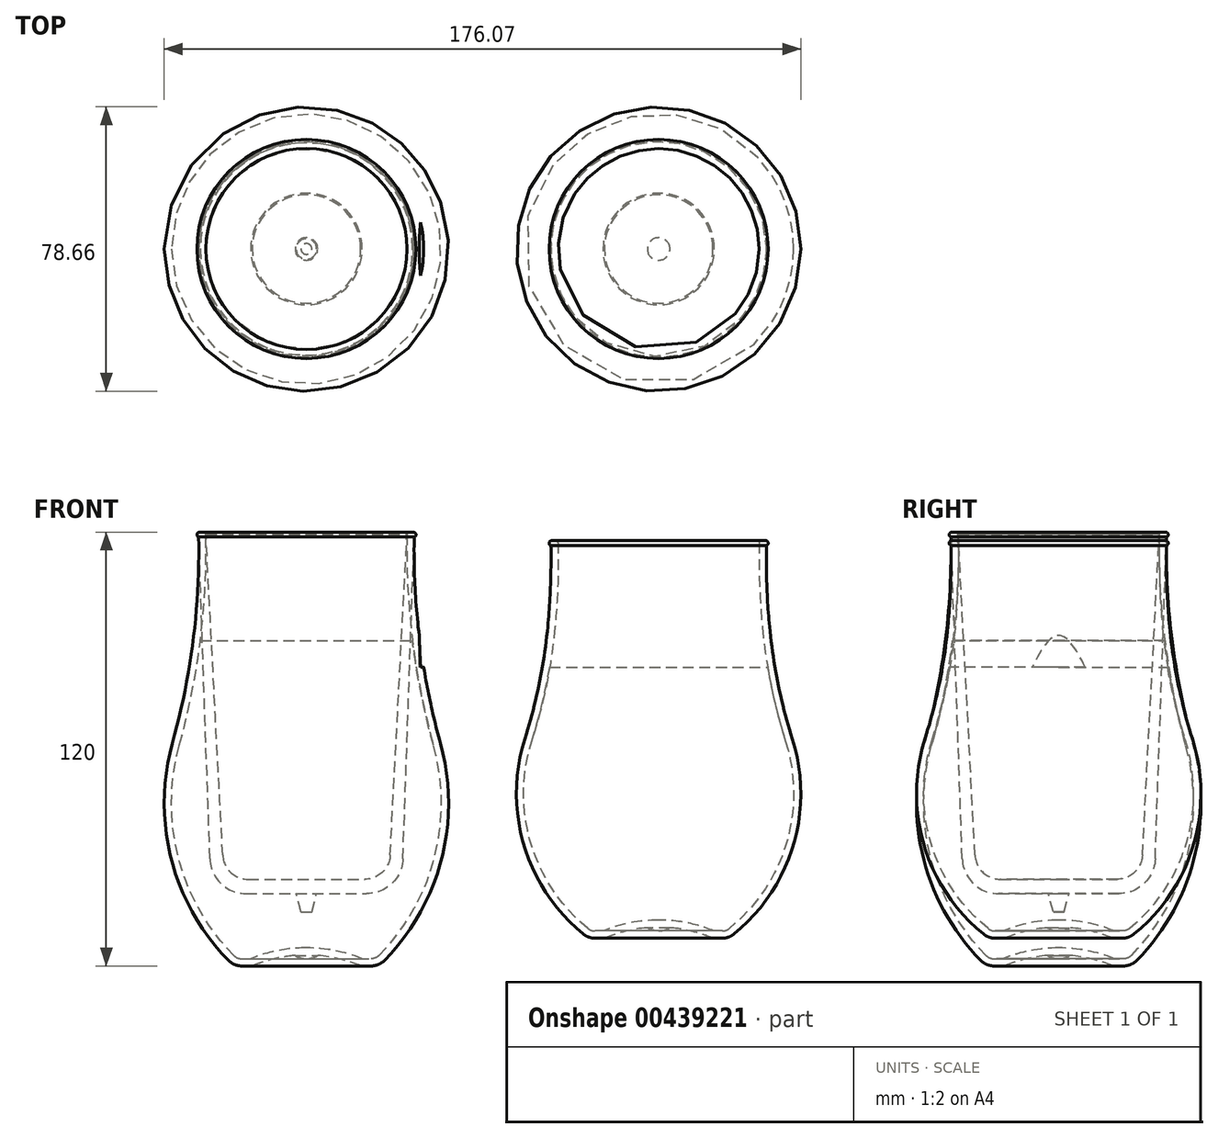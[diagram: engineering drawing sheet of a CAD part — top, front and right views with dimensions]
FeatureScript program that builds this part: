
annotation { "Feature Type Name" : "Feature", "Feature Type Description" : "" }
export const myFeature = defineFeature(function(context is Context, id is Id, definition is map)
    precondition{}
    {
        {
            var Q0;
            Q0=qCreatedBy(makeId("Front.planeOp"),FACE);
            var sketch = newSketch(context, id + "F0", { "sketchPlane" : qUnion([Q0])});
            skLineSegment(sketch, "E0", {"start": v(-17.96, -60) * mm, "end": v(0, -60) * mm});
            skArc(sketch, "E1", {"start": v(-37.07, 1.6) * mm, "mid": v(-37.35, -30.53) * mm, "end": v(-21.52, -58.5) * mm});
            skArc(sketch, "E2", {"start": v(-37.07, 1.6) * mm, "mid": v(-31.37, 29.87) * mm, "end": v(-29.8, 58.66) * mm});
            skArc(sketch, "E3", {"start": v(-21.52, -58.5) * mm, "mid": v(-19.89, -59.61) * mm, "end": v(-17.96, -60) * mm});
            skArc(sketch, "E4", {"start": v(-3.12, -57.12) * mm, "mid": v(-1.62, -57.78) * mm, "end": v(0, -58) * mm});
            skArc(sketch, "E5", {"start": v(-3.12, -57.13) * mm, "mid": v(-9.17, -58.1) * mm, "end": v(-15, -60) * mm});
            skArc(sketch, "E6", {"start": v(-35.14, 1.07) * mm, "mid": v(-29.34, 29.97) * mm, "end": v(-27.81, 59.41) * mm});
            skArc(sketch, "E7", {"start": v(-35.14, 1.07) * mm, "mid": v(-35.42, -30.03) * mm, "end": v(-20.1, -57.1) * mm});
            skArc(sketch, "E8", {"start": v(0, -55) * mm, "mid": v(-7.84, -55.76) * mm, "end": v(-15.4, -58) * mm});
            skLineSegment(sketch, "E9", {"start": v(-17.96, -58) * mm, "end": v(-15.4, -58) * mm});
            skArc(sketch, "E10", {"start": v(-20.1, -57.1) * mm, "mid": v(-19.12, -57.77) * mm, "end": v(-17.96, -58) * mm});
            skArc(sketch, "E11", {"start": v(-30.3, 59.25) * mm, "mid": v(-30.16, 58.86) * mm, "end": v(-29.8, 58.66) * mm});
            skArc(sketch, "E12", {"start": v(-29.55, 60) * mm, "mid": v(-30.08, 59.78) * mm, "end": v(-30.3, 59.25) * mm});
            skArc(sketch, "E13", {"start": v(-27.81, 59.41) * mm, "mid": v(-28, 59.83) * mm, "end": v(-28.41, 60) * mm});
            skLineSegment(sketch, "E14", {"start": v(-29.55, 60) * mm, "end": v(-28.41, 60) * mm});
            skLineSegment(sketch, "E15", {"start": v(-28.41, 60) * mm, "end": v(0, 60) * mm});
            skLineSegment(sketch, "E16", {"start": v(17.96, -60) * mm, "end": v(0, -60) * mm});
            skArc(sketch, "E17", {"start": v(21.52, -58.5) * mm, "mid": v(37.35, -30.53) * mm, "end": v(37.07, 1.6) * mm});
            skArc(sketch, "E18", {"start": v(17.96, -60) * mm, "mid": v(19.89, -59.61) * mm, "end": v(21.52, -58.5) * mm});
            skArc(sketch, "E19", {"start": v(0, -58) * mm, "mid": v(1.62, -57.78) * mm, "end": v(3.12, -57.12) * mm});
            skArc(sketch, "E20", {"start": v(15, -60) * mm, "mid": v(9.17, -58.1) * mm, "end": v(3.12, -57.13) * mm});
            skArc(sketch, "E21", {"start": v(27.81, 59.41) * mm, "mid": v(29.34, 29.97) * mm, "end": v(35.14, 1.07) * mm});
            skArc(sketch, "E22", {"start": v(20.1, -57.1) * mm, "mid": v(35.42, -30.03) * mm, "end": v(35.14, 1.07) * mm});
            skArc(sketch, "E23", {"start": v(15.4, -58) * mm, "mid": v(7.84, -55.76) * mm, "end": v(0, -55) * mm});
            skLineSegment(sketch, "E24", {"start": v(17.96, -58) * mm, "end": v(15.4, -58) * mm});
            skArc(sketch, "E25", {"start": v(17.96, -58) * mm, "mid": v(19.12, -57.77) * mm, "end": v(20.1, -57.1) * mm});
            skArc(sketch, "E26", {"start": v(29.8, 58.66) * mm, "mid": v(30.16, 58.86) * mm, "end": v(30.3, 59.25) * mm});
            skArc(sketch, "E27", {"start": v(30.3, 59.25) * mm, "mid": v(30.08, 59.78) * mm, "end": v(29.55, 60) * mm});
            skArc(sketch, "E28", {"start": v(28.41, 60) * mm, "mid": v(28, 59.83) * mm, "end": v(27.81, 59.41) * mm});
            skLineSegment(sketch, "E29", {"start": v(29.55, 60) * mm, "end": v(28.41, 60) * mm});
            skArc(sketch, "E30", {"start": v(29.8, 58.66) * mm, "mid": v(31.37, 29.87) * mm, "end": v(37.07, 1.6) * mm});
            skLineSegment(sketch, "E31", {"start": v(28.41, 60) * mm, "end": v(0, 60) * mm});
            skSolve(sketch);
        }
        {
            var Q0;
            Q0=qCreatedBy(makeId("Front.planeOp"),FACE);
            var sketch = newSketch(context, id + "F1", { "sketchPlane" : qUnion([Q0])});
            skArc(sketch, "E32.0", {"start": v(-35.14, 1.07) * mm, "mid": v(-29.34, 29.97) * mm, "end": v(-27.81, 59.41) * mm});
            skArc(sketch, "E33.0", {"start": v(-27.81, 59.41) * mm, "mid": v(-28, 59.83) * mm, "end": v(-28.41, 60) * mm});
            skLineSegment(sketch, "E34.0", {"start": v(-28.41, 60) * mm, "end": v(0, 60) * mm});
            skArc(sketch, "E35.0", {"start": v(-35.14, 1.07) * mm, "mid": v(-35.42, -30.03) * mm, "end": v(-20.1, -57.1) * mm});
            skArc(sketch, "E36.0", {"start": v(-20.1, -57.1) * mm, "mid": v(-19.12, -57.77) * mm, "end": v(-17.96, -58) * mm});
            skLineSegment(sketch, "E37.0", {"start": v(-17.96, -58) * mm, "end": v(-15.4, -58) * mm});
            skArc(sketch, "E38.0", {"start": v(0, -55) * mm, "mid": v(-7.84, -55.76) * mm, "end": v(-15.4, -58) * mm});
            skLineSegment(sketch, "E39", {"start": v(0, -55) * mm, "end": v(0, 60) * mm});
            skSolve(sketch);
        }
        {
            var Q0;
            Q0 = qSketchRegion(id + "F1", true);
            var Q1;
            Q1=sQuery(id+"F1.wireOp",EDGE,"E39");
            revolve(context, id + "F2", {"entities" : qUnion([Q0]), "axis" : qUnion([Q1]), "revolveType" : RevolveType.FULL});
        }
        {
            var Q0;
            Q0=makeQuery(id+"F2.opRevolve","SWEPT_FACE",FACE,{"disambiguationData":[OSD([sQuery(id+"F1.wireOp",EDGE,"E34.0")])]});
            var sketch = newSketch(context, id + "F3", { "sketchPlane" : qUnion([Q0])});
            skCircle(sketch, "E40", {"center": v(0, 0) * mm, "radius": 125.99 * mm});
            skSolve(sketch);
        }
        {
            var Q0;
            Q0 = qSketchRegion(id + "F3", true);
            extrude(context, id + "F4", {"entities" : qUnion([Q0]), "operationType" : NewBodyOperationType.REMOVE, "oppositeDirection" : true, "depth" : 30 * mm});
        }
        {
            var Q0;
            Q0=qCreatedBy(makeId("Front.planeOp"),FACE);
            var sketch = newSketch(context, id + "F5", { "sketchPlane" : qUnion([Q0])});
            skArc(sketch, "E41.0", {"start": v(-27.81, 59.41) * mm, "mid": v(-28, 59.83) * mm, "end": v(-28.41, 60) * mm});
            skLineSegment(sketch, "E42.0", {"start": v(-29.55, 60) * mm, "end": v(-28.41, 60) * mm});
            skArc(sketch, "E43.0", {"start": v(-29.55, 60) * mm, "mid": v(-30.08, 59.78) * mm, "end": v(-30.3, 59.25) * mm});
            skArc(sketch, "E44.0", {"start": v(-30.3, 59.25) * mm, "mid": v(-30.16, 58.86) * mm, "end": v(-29.8, 58.66) * mm});
            skArc(sketch, "E45.0", {"start": v(-37.07, 1.6) * mm, "mid": v(-31.37, 29.87) * mm, "end": v(-29.8, 58.66) * mm});
            skArc(sketch, "E46.0", {"start": v(-35.14, 1.07) * mm, "mid": v(-29.34, 29.97) * mm, "end": v(-27.81, 59.41) * mm});
            skArc(sketch, "E47.0", {"start": v(-35.14, 1.07) * mm, "mid": v(-35.42, -30.03) * mm, "end": v(-20.1, -57.1) * mm});
            skArc(sketch, "E48.0", {"start": v(-37.07, 1.6) * mm, "mid": v(-37.35, -30.53) * mm, "end": v(-21.52, -58.5) * mm});
            skArc(sketch, "E49.0", {"start": v(-20.1, -57.1) * mm, "mid": v(-19.12, -57.77) * mm, "end": v(-17.96, -58) * mm});
            skArc(sketch, "E50.0", {"start": v(-21.52, -58.5) * mm, "mid": v(-19.89, -59.61) * mm, "end": v(-17.96, -60) * mm});
            skLineSegment(sketch, "E51.0", {"start": v(-17.96, -58) * mm, "end": v(-15.4, -58) * mm});
            skArc(sketch, "E52.0", {"start": v(0, -55) * mm, "mid": v(-7.84, -55.76) * mm, "end": v(-15.4, -58) * mm});
            skArc(sketch, "E53.0", {"start": v(-3.12, -57.13) * mm, "mid": v(-9.17, -58.1) * mm, "end": v(-15, -60) * mm});
            skArc(sketch, "E54.0", {"start": v(-3.12, -57.12) * mm, "mid": v(-1.62, -57.78) * mm, "end": v(0, -58) * mm});
            skLineSegment(sketch, "E55", {"start": v(-17.96, -60) * mm, "end": v(-15, -60) * mm});
            skLineSegment(sketch, "E56", {"start": v(0, -58) * mm, "end": v(0, -55) * mm});
            skSolve(sketch);
        }
        {
            var Q0;
            Q0 = qSketchRegion(id + "F5", true);
            var Q1;
            Q1=sQuery(id+"F5.wireOp",EDGE,"E56");
            revolve(context, id + "F6", {"entities" : qUnion([Q0]), "axis" : qUnion([Q1]), "revolveType" : RevolveType.FULL});
        }
        {
            var Q0;
            Q0=qCreatedBy(makeId("Front.planeOp"),FACE);
            var sketch = newSketch(context, id + "F7", { "sketchPlane" : qUnion([Q0])});
            skArc(sketch, "E57.0", {"start": v(-27.81, 59.41) * mm, "mid": v(-28, 59.83) * mm, "end": v(-28.41, 60) * mm});
            skLineSegment(sketch, "E58.0", {"start": v(-29.55, 60) * mm, "end": v(-28.41, 60) * mm});
            skArc(sketch, "E59.0", {"start": v(-29.55, 60) * mm, "mid": v(-30.08, 59.78) * mm, "end": v(-30.3, 59.25) * mm});
            skArc(sketch, "E60.0", {"start": v(-30.3, 59.25) * mm, "mid": v(-30.16, 58.86) * mm, "end": v(-29.8, 58.66) * mm});
            skLineSegment(sketch, "E61", {"start": v(-29.8, 58.66) * mm, "end": v(-26.7, -30.35) * mm});
            skLineSegment(sketch, "E62", {"start": v(-16.7, -40) * mm, "end": v(-2.84, -40) * mm});
            skLineSegment(sketch, "E63", {"start": v(0, -40) * mm, "end": v(0, -36) * mm});
            skLineSegment(sketch, "E64", {"start": v(0, -36) * mm, "end": v(-16.17, -36) * mm});
            skLineSegment(sketch, "E65", {"start": v(-23.16, -29.37) * mm, "end": v(-27.81, 59.41) * mm});
            skLineSegment(sketch, "E66", {"start": v(0, -40) * mm, "end": v(0, -45) * mm});
            skLineSegment(sketch, "E67", {"start": v(0, -45) * mm, "end": v(-1.5, -45) * mm});
            skLineSegment(sketch, "E68", {"start": v(-1.5, -45) * mm, "end": v(-2.84, -40) * mm});
            skPoint(sketch, "E69.visualSharp", {"position": v(-22.81, -36) * mm});
            skArc(sketch, "E69.filletArc", {"start": v(-23.16, -29.37) * mm, "mid": v(-21, -34.08) * mm, "end": v(-16.17, -36) * mm});
            skPoint(sketch, "E70.visualSharp", {"position": v(-26.36, -40) * mm});
            skArc(sketch, "E70.filletArc", {"start": v(-26.7, -30.35) * mm, "mid": v(-23.65, -37.2) * mm, "end": v(-16.7, -40) * mm});
            skSolve(sketch);
        }
        {
            var Q0;
            Q0 = qSketchRegion(id + "F7", true);
            var Q1;
            Q1=sQuery(id+"F7.wireOp",EDGE,"E63");
            revolve(context, id + "F8", {"entities" : qUnion([Q0]), "axis" : qUnion([Q1]), "revolveType" : RevolveType.FULL});
        }
        {
            var Q0;
            Q0=qCreatedBy(makeId("Front.planeOp"),FACE);
            var sketch = newSketch(context, id + "F9", { "sketchPlane" : qUnion([Q0])});
            skLineSegment(sketch, "E71", {"start": v(-115.37, -60) * mm, "end": v(-97.41, -60) * mm});
            skArc(sketch, "E72", {"start": v(-134.48, 1.6) * mm, "mid": v(-134.77, -30.53) * mm, "end": v(-118.94, -58.5) * mm});
            skArc(sketch, "E73", {"start": v(-134.48, 1.6) * mm, "mid": v(-128.79, 29.87) * mm, "end": v(-127.22, 58.66) * mm});
            skArc(sketch, "E74", {"start": v(-118.94, -58.5) * mm, "mid": v(-117.3, -59.61) * mm, "end": v(-115.37, -60) * mm});
            skArc(sketch, "E75", {"start": v(-100.53, -57.12) * mm, "mid": v(-99.03, -57.78) * mm, "end": v(-97.41, -58) * mm});
            skArc(sketch, "E76", {"start": v(-100.53, -57.13) * mm, "mid": v(-106.59, -58.1) * mm, "end": v(-112.41, -60) * mm});
            skArc(sketch, "E77", {"start": v(-132.55, 1.07) * mm, "mid": v(-126.76, 29.97) * mm, "end": v(-125.23, 59.41) * mm});
            skArc(sketch, "E78", {"start": v(-132.55, 1.07) * mm, "mid": v(-132.83, -30.03) * mm, "end": v(-117.5, -57.1) * mm});
            skArc(sketch, "E79", {"start": v(-97.41, -55) * mm, "mid": v(-105.26, -55.76) * mm, "end": v(-112.8, -58) * mm});
            skLineSegment(sketch, "E80", {"start": v(-115.37, -58) * mm, "end": v(-112.8, -58) * mm});
            skArc(sketch, "E81", {"start": v(-117.5, -57.1) * mm, "mid": v(-116.53, -57.77) * mm, "end": v(-115.37, -58) * mm});
            skArc(sketch, "E82", {"start": v(-127.71, 59.25) * mm, "mid": v(-127.57, 58.86) * mm, "end": v(-127.22, 58.66) * mm});
            skArc(sketch, "E83", {"start": v(-126.96, 60) * mm, "mid": v(-127.5, 59.78) * mm, "end": v(-127.71, 59.25) * mm});
            skArc(sketch, "E84", {"start": v(-125.23, 59.41) * mm, "mid": v(-125.4, 59.83) * mm, "end": v(-125.83, 60) * mm});
            skLineSegment(sketch, "E85", {"start": v(-126.96, 60) * mm, "end": v(-125.83, 60) * mm});
            skLineSegment(sketch, "E86", {"start": v(-125.83, 60) * mm, "end": v(-97.41, 60) * mm});
            skLineSegment(sketch, "E87", {"start": v(-79.46, -60) * mm, "end": v(-97.41, -60) * mm});
            skArc(sketch, "E88", {"start": v(-75.9, -58.5) * mm, "mid": v(-60.06, -30.53) * mm, "end": v(-60.35, 1.6) * mm});
            skArc(sketch, "E89", {"start": v(-79.46, -60) * mm, "mid": v(-77.53, -59.61) * mm, "end": v(-75.9, -58.5) * mm});
            skArc(sketch, "E90", {"start": v(-97.41, -58) * mm, "mid": v(-95.8, -57.78) * mm, "end": v(-94.3, -57.12) * mm});
            skArc(sketch, "E91", {"start": v(-82.41, -60) * mm, "mid": v(-88.24, -58.1) * mm, "end": v(-94.3, -57.13) * mm});
            skArc(sketch, "E92", {"start": v(-69.6, 59.41) * mm, "mid": v(-68.07, 29.97) * mm, "end": v(-62.27, 1.07) * mm});
            skArc(sketch, "E93", {"start": v(-77.32, -57.1) * mm, "mid": v(-62, -30.03) * mm, "end": v(-62.27, 1.07) * mm});
            skArc(sketch, "E94", {"start": v(-82.02, -58) * mm, "mid": v(-89.57, -55.76) * mm, "end": v(-97.41, -55) * mm});
            skLineSegment(sketch, "E95", {"start": v(-79.46, -58) * mm, "end": v(-82.02, -58) * mm});
            skArc(sketch, "E96", {"start": v(-79.46, -58) * mm, "mid": v(-78.3, -57.77) * mm, "end": v(-77.32, -57.1) * mm});
            skArc(sketch, "E97", {"start": v(-67.61, 58.66) * mm, "mid": v(-67.26, 58.86) * mm, "end": v(-67.12, 59.25) * mm});
            skArc(sketch, "E98", {"start": v(-67.12, 59.25) * mm, "mid": v(-67.34, 59.78) * mm, "end": v(-67.87, 60) * mm});
            skArc(sketch, "E99", {"start": v(-69, 60) * mm, "mid": v(-69.42, 59.83) * mm, "end": v(-69.6, 59.41) * mm});
            skLineSegment(sketch, "E100", {"start": v(-67.87, 60) * mm, "end": v(-69, 60) * mm});
            skArc(sketch, "E101", {"start": v(-67.61, 58.66) * mm, "mid": v(-66.04, 29.87) * mm, "end": v(-60.35, 1.6) * mm});
            skLineSegment(sketch, "E102", {"start": v(-69, 60) * mm, "end": v(-97.41, 60) * mm});
            skLineSegment(sketch, "E103", {"start": v(-68.07, 30) * mm, "end": v(-126.75, 30) * mm});
            skLineSegment(sketch, "E104", {"start": v(-123.76, -40.35) * mm, "end": v(-127.22, 58.66) * mm});
            skLineSegment(sketch, "E105", {"start": v(-113.76, -50) * mm, "end": v(-100.25, -50) * mm});
            skArc(sketch, "E106", {"start": v(-123.76, -40.35) * mm, "mid": v(-120.71, -47.2) * mm, "end": v(-113.76, -50) * mm});
            skLineSegment(sketch, "E107", {"start": v(-113.5, -46) * mm, "end": v(-97.41, -46) * mm});
            skLineSegment(sketch, "E108", {"start": v(-100.25, -50) * mm, "end": v(-98.91, -55) * mm});
            skLineSegment(sketch, "E109", {"start": v(-98.91, -55) * mm, "end": v(-97.41, -55) * mm});
            skLineSegment(sketch, "E110", {"start": v(-120.49, -39.34) * mm, "end": v(-125.23, 59.45) * mm});
            skArc(sketch, "E111", {"start": v(-120.49, -39.34) * mm, "mid": v(-118.32, -44.07) * mm, "end": v(-113.5, -46) * mm});
            skArc(sketch, "E112", {"start": v(94.3, -49.45) * mm, "mid": v(95.8, -50.1) * mm, "end": v(97.41, -50.32) * mm});
            skArc(sketch, "E113", {"start": v(94.3, -49.45) * mm, "mid": v(88.24, -50.42) * mm, "end": v(82.41, -52.32) * mm});
            skArc(sketch, "E114", {"start": v(97.41, -47.32) * mm, "mid": v(89.57, -48.08) * mm, "end": v(82.02, -50.32) * mm});
            skLineSegment(sketch, "E115", {"start": v(79.77, -50.32) * mm, "end": v(82.02, -50.32) * mm});
            skArc(sketch, "E116", {"start": v(67.12, 56.93) * mm, "mid": v(67.26, 56.54) * mm, "end": v(67.61, 56.33) * mm});
            skArc(sketch, "E117", {"start": v(67.87, 57.68) * mm, "mid": v(67.34, 57.46) * mm, "end": v(67.12, 56.93) * mm});
            skArc(sketch, "E118", {"start": v(66.74, 33.85) * mm, "mid": v(67.5, 45.08) * mm, "end": v(67.61, 56.33) * mm});
            skLineSegment(sketch, "E119", {"start": v(79.77, -52.32) * mm, "end": v(82.41, -52.32) * mm});
            skArc(sketch, "E120", {"start": v(60.42, 2.78) * mm, "mid": v(60.2, -26.71) * mm, "end": v(76.63, -51.2) * mm});
            skArc(sketch, "E121", {"start": v(76.63, -51.2) * mm, "mid": v(78.1, -52.04) * mm, "end": v(79.77, -52.32) * mm});
            skArc(sketch, "E122", {"start": v(60.42, 2.78) * mm, "mid": v(64.4, 18.15) * mm, "end": v(66.74, 33.85) * mm});
            skArc(sketch, "E123", {"start": v(68.74, 33.66) * mm, "mid": v(69.5, 45.36) * mm, "end": v(69.6, 57.09) * mm});
            skArc(sketch, "E124", {"start": v(62.33, 2.18) * mm, "mid": v(66.37, 17.75) * mm, "end": v(68.74, 33.66) * mm});
            skArc(sketch, "E125", {"start": v(62.33, 2.18) * mm, "mid": v(62.11, -26.14) * mm, "end": v(77.89, -49.66) * mm});
            skArc(sketch, "E126", {"start": v(77.89, -49.66) * mm, "mid": v(78.77, -50.15) * mm, "end": v(79.77, -50.32) * mm});
            skArc(sketch, "E127", {"start": v(69.6, 57.09) * mm, "mid": v(69.42, 57.5) * mm, "end": v(69, 57.68) * mm});
            skLineSegment(sketch, "E128", {"start": v(67.87, 57.68) * mm, "end": v(69, 57.68) * mm});
            skLineSegment(sketch, "E129", {"start": v(69, 57.68) * mm, "end": v(97.41, 57.68) * mm});
            skArc(sketch, "E130", {"start": v(127.22, 56.33) * mm, "mid": v(127.57, 56.54) * mm, "end": v(127.71, 56.93) * mm});
            skArc(sketch, "E131", {"start": v(127.71, 56.93) * mm, "mid": v(127.5, 57.46) * mm, "end": v(126.96, 57.68) * mm});
            skArc(sketch, "E132", {"start": v(127.22, 56.33) * mm, "mid": v(127.33, 45.08) * mm, "end": v(128.08, 33.85) * mm});
            skArc(sketch, "E133", {"start": v(125.23, 57.09) * mm, "mid": v(125.32, 45.36) * mm, "end": v(126.1, 33.66) * mm});
            skArc(sketch, "E134", {"start": v(125.83, 57.68) * mm, "mid": v(125.4, 57.5) * mm, "end": v(125.23, 57.09) * mm});
            skLineSegment(sketch, "E135", {"start": v(126.96, 57.68) * mm, "end": v(125.83, 57.68) * mm});
            skLineSegment(sketch, "E136", {"start": v(125.83, 57.68) * mm, "end": v(97.41, 57.68) * mm});
            skArc(sketch, "E137", {"start": v(118.2, -51.2) * mm, "mid": v(134.63, -26.71) * mm, "end": v(134.4, 2.78) * mm});
            skArc(sketch, "E138", {"start": v(128.08, 33.85) * mm, "mid": v(130.42, 18.15) * mm, "end": v(134.4, 2.78) * mm});
            skArc(sketch, "E139", {"start": v(126.1, 33.66) * mm, "mid": v(128.46, 17.75) * mm, "end": v(132.5, 2.18) * mm});
            skArc(sketch, "E140", {"start": v(116.94, -49.66) * mm, "mid": v(132.72, -26.14) * mm, "end": v(132.5, 2.18) * mm});
            skArc(sketch, "E141", {"start": v(97.41, -50.32) * mm, "mid": v(99.03, -50.1) * mm, "end": v(100.53, -49.45) * mm});
            skArc(sketch, "E142", {"start": v(112.41, -52.32) * mm, "mid": v(106.59, -50.42) * mm, "end": v(100.53, -49.45) * mm});
            skArc(sketch, "E143", {"start": v(112.8, -50.32) * mm, "mid": v(105.26, -48.08) * mm, "end": v(97.41, -47.32) * mm});
            skLineSegment(sketch, "E144", {"start": v(115.06, -52.32) * mm, "end": v(112.41, -52.32) * mm});
            skArc(sketch, "E145", {"start": v(115.06, -52.32) * mm, "mid": v(116.72, -52.04) * mm, "end": v(118.2, -51.2) * mm});
            skArc(sketch, "E146", {"start": v(115.06, -50.32) * mm, "mid": v(116.06, -50.15) * mm, "end": v(116.94, -49.66) * mm});
            skLineSegment(sketch, "E147", {"start": v(115.06, -50.32) * mm, "end": v(112.8, -50.32) * mm});
            skLineSegment(sketch, "E148", {"start": v(82.41, -52.32) * mm, "end": v(112.41, -52.32) * mm});
            skSolve(sketch);
        }
        {
            var Q0;
            Q0=qCreatedBy(makeId("Front.planeOp"),FACE);
            var sketch = newSketch(context, id + "F10", { "sketchPlane" : qUnion([Q0])});
            skArc(sketch, "E149.0", {"start": v(69.6, 57.09) * mm, "mid": v(69.42, 57.5) * mm, "end": v(69, 57.68) * mm});
            skArc(sketch, "E150.0", {"start": v(68.74, 33.66) * mm, "mid": v(69.5, 45.36) * mm, "end": v(69.6, 57.09) * mm});
            skArc(sketch, "E151.0", {"start": v(62.33, 2.18) * mm, "mid": v(66.37, 17.75) * mm, "end": v(68.74, 33.66) * mm});
            skArc(sketch, "E152.0", {"start": v(62.33, 2.18) * mm, "mid": v(62.11, -26.14) * mm, "end": v(77.89, -49.66) * mm});
            skArc(sketch, "E153.0", {"start": v(77.89, -49.66) * mm, "mid": v(78.77, -50.15) * mm, "end": v(79.77, -50.32) * mm});
            skLineSegment(sketch, "E154.0", {"start": v(79.77, -50.32) * mm, "end": v(82.02, -50.32) * mm});
            skArc(sketch, "E155.0", {"start": v(97.41, -47.32) * mm, "mid": v(89.57, -48.08) * mm, "end": v(82.02, -50.32) * mm});
            skLineSegment(sketch, "E156.0", {"start": v(69, 57.68) * mm, "end": v(97.41, 57.68) * mm});
            skLineSegment(sketch, "E157", {"start": v(97.41, 57.68) * mm, "end": v(97.41, -47.32) * mm});
            skSolve(sketch);
        }
        {
            var Q0;
            Q0 = qSketchRegion(id + "F10", true);
            var Q1;
            Q1=sQuery(id+"F10.wireOp",EDGE,"E157");
            revolve(context, id + "F11", {"entities" : qUnion([Q0]), "axis" : qUnion([Q1]), "revolveType" : RevolveType.FULL});
        }
        {
            var Q0;
            Q0=makeQuery(id+"F11.opRevolve","SWEPT_FACE",FACE,{"disambiguationData":[OSD([sQuery(id+"F10.wireOp",EDGE,"E156.0")])]});
            var sketch = newSketch(context, id + "F12", { "sketchPlane" : qUnion([Q0])});
            skCircle(sketch, "E158", {"center": v(97.41, 0) * mm, "radius": 66.23 * mm});
            skSolve(sketch);
        }
        {
            var Q0;
            Q0 = qSketchRegion(id + "F12", true);
            extrude(context, id + "F13", {"entities" : qUnion([Q0]), "operationType" : NewBodyOperationType.REMOVE, "oppositeDirection" : true, "depth" : 35 * mm});
        }
        {
            var Q0;
            Q0=qCreatedBy(makeId("Front.planeOp"),FACE);
            var sketch = newSketch(context, id + "F14", { "sketchPlane" : qUnion([Q0])});
            skArc(sketch, "E159.0", {"start": v(69.6, 57.09) * mm, "mid": v(69.42, 57.5) * mm, "end": v(69, 57.68) * mm});
            skArc(sketch, "E160.0", {"start": v(68.74, 33.66) * mm, "mid": v(69.5, 45.36) * mm, "end": v(69.6, 57.09) * mm});
            skLineSegment(sketch, "E161.0", {"start": v(67.87, 57.68) * mm, "end": v(69, 57.68) * mm});
            skArc(sketch, "E162.0", {"start": v(67.87, 57.68) * mm, "mid": v(67.34, 57.46) * mm, "end": v(67.12, 56.93) * mm});
            skArc(sketch, "E163.0", {"start": v(67.12, 56.93) * mm, "mid": v(67.26, 56.54) * mm, "end": v(67.61, 56.33) * mm});
            skArc(sketch, "E164.0", {"start": v(66.74, 33.85) * mm, "mid": v(67.5, 45.08) * mm, "end": v(67.61, 56.33) * mm});
            skArc(sketch, "E165.0", {"start": v(62.33, 2.18) * mm, "mid": v(66.37, 17.75) * mm, "end": v(68.74, 33.66) * mm});
            skArc(sketch, "E166.0", {"start": v(60.42, 2.78) * mm, "mid": v(64.4, 18.15) * mm, "end": v(66.74, 33.85) * mm});
            skArc(sketch, "E167.0", {"start": v(60.42, 2.78) * mm, "mid": v(60.2, -26.71) * mm, "end": v(76.63, -51.2) * mm});
            skArc(sketch, "E168.0", {"start": v(62.33, 2.18) * mm, "mid": v(62.11, -26.14) * mm, "end": v(77.89, -49.66) * mm});
            skArc(sketch, "E169.0", {"start": v(77.89, -49.66) * mm, "mid": v(78.77, -50.15) * mm, "end": v(79.77, -50.32) * mm});
            skArc(sketch, "E170.0", {"start": v(76.63, -51.2) * mm, "mid": v(78.1, -52.04) * mm, "end": v(79.77, -52.32) * mm});
            skLineSegment(sketch, "E171.0", {"start": v(79.77, -50.32) * mm, "end": v(82.02, -50.32) * mm});
            skLineSegment(sketch, "E172.0", {"start": v(79.77, -52.32) * mm, "end": v(82.41, -52.32) * mm});
            skArc(sketch, "E173.0", {"start": v(94.3, -49.45) * mm, "mid": v(88.24, -50.42) * mm, "end": v(82.41, -52.32) * mm});
            skArc(sketch, "E174.0", {"start": v(97.41, -47.32) * mm, "mid": v(89.57, -48.08) * mm, "end": v(82.02, -50.32) * mm});
            skArc(sketch, "E175.0", {"start": v(94.3, -49.45) * mm, "mid": v(95.8, -50.1) * mm, "end": v(97.41, -50.32) * mm});
            skLineSegment(sketch, "E176", {"start": v(97.41, -47.32) * mm, "end": v(97.41, -50.32) * mm});
            skSolve(sketch);
        }
        {
            var Q0;
            Q0 = qSketchRegion(id + "F14", true);
            var Q1;
            Q1=sQuery(id+"F14.wireOp",EDGE,"E176");
            revolve(context, id + "F15", {"entities" : qUnion([Q0]), "axis" : qUnion([Q1]), "revolveType" : RevolveType.FULL});
        }
    });
